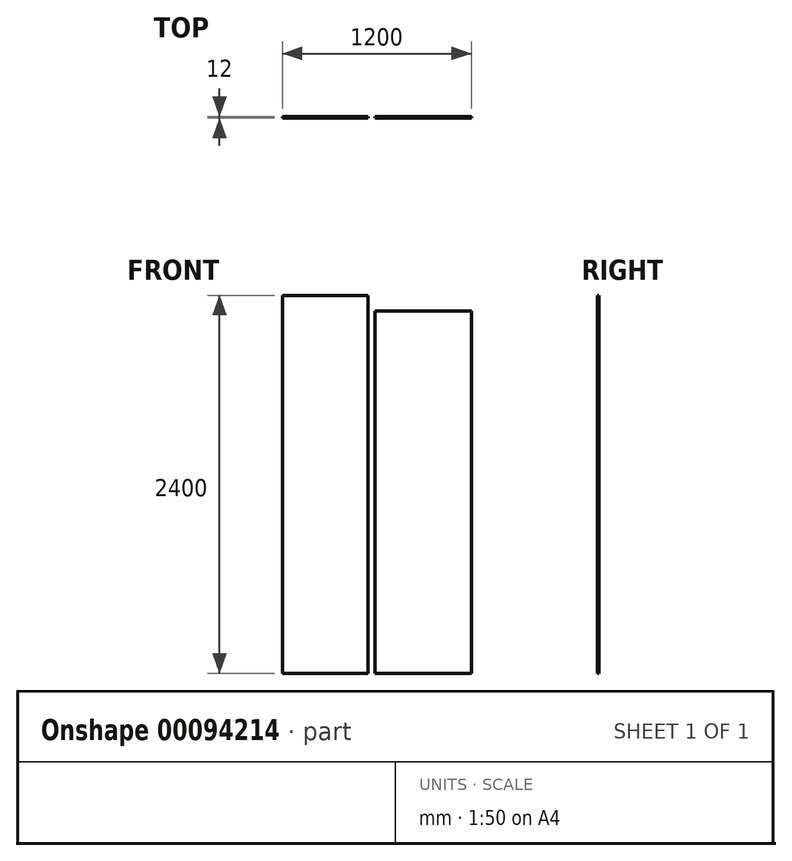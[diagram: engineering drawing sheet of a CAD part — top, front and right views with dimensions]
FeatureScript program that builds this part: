
annotation { "Feature Type Name" : "Feature", "Feature Type Description" : "" }
export const myFeature = defineFeature(function(context is Context, id is Id, definition is map)
    precondition{}
    {
        {
            var Q0;
            Q0=qCreatedBy(makeId("Front.planeOp"),FACE);
            var sketch = newSketch(context, id + "F0", { "sketchPlane" : qUnion([Q0])});
            skLineSegment(sketch, "E0.bottom", {"start": v(600, -1200) * mm, "end": v(-600, -1200) * mm});
            skLineSegment(sketch, "E0.top", {"start": v(600, 1200) * mm, "end": v(-600, 1200) * mm});
            skLineSegment(sketch, "E0.left", {"start": v(600, -1200) * mm, "end": v(600, 1200) * mm});
            skLineSegment(sketch, "E0.right", {"start": v(-600, -1200) * mm, "end": v(-600, 1200) * mm});
            skPoint(sketch, "E0.middle", {"position": v(0, 0) * mm});
            skLineSegment(sketch, "E1", {"start": v(-12, -1200) * mm, "end": v(-12, 1100) * mm});
            skLineSegment(sketch, "E2", {"start": v(-328, -1200) * mm, "end": v(-328, 1200) * mm});
            skLineSegment(sketch, "E3", {"start": v(-56, -1200) * mm, "end": v(-56, 1200) * mm});
            skLineSegment(sketch, "E4", {"start": v(-12, 1100) * mm, "end": v(600, 1100) * mm});
            skSolve(sketch);
        }
        {
            var Q0;
            Q0=makeQuery(id+"F0.imprint","IMPRINT",FACE,{"disambiguationData":[TD([[makeQuery(id+"F0.imprint","IMPRINT",EDGE,{"derivedFrom":sQuery(id+"F0.wireOp",EDGE,"E0.bottom")}),-1.0]])]});
            extrude(context, id + "F1", {"entities" : qUnion([Q0]), "endBound" : BoundingType.SYMMETRIC, "depth" : 12 * mm});
        }
    });
